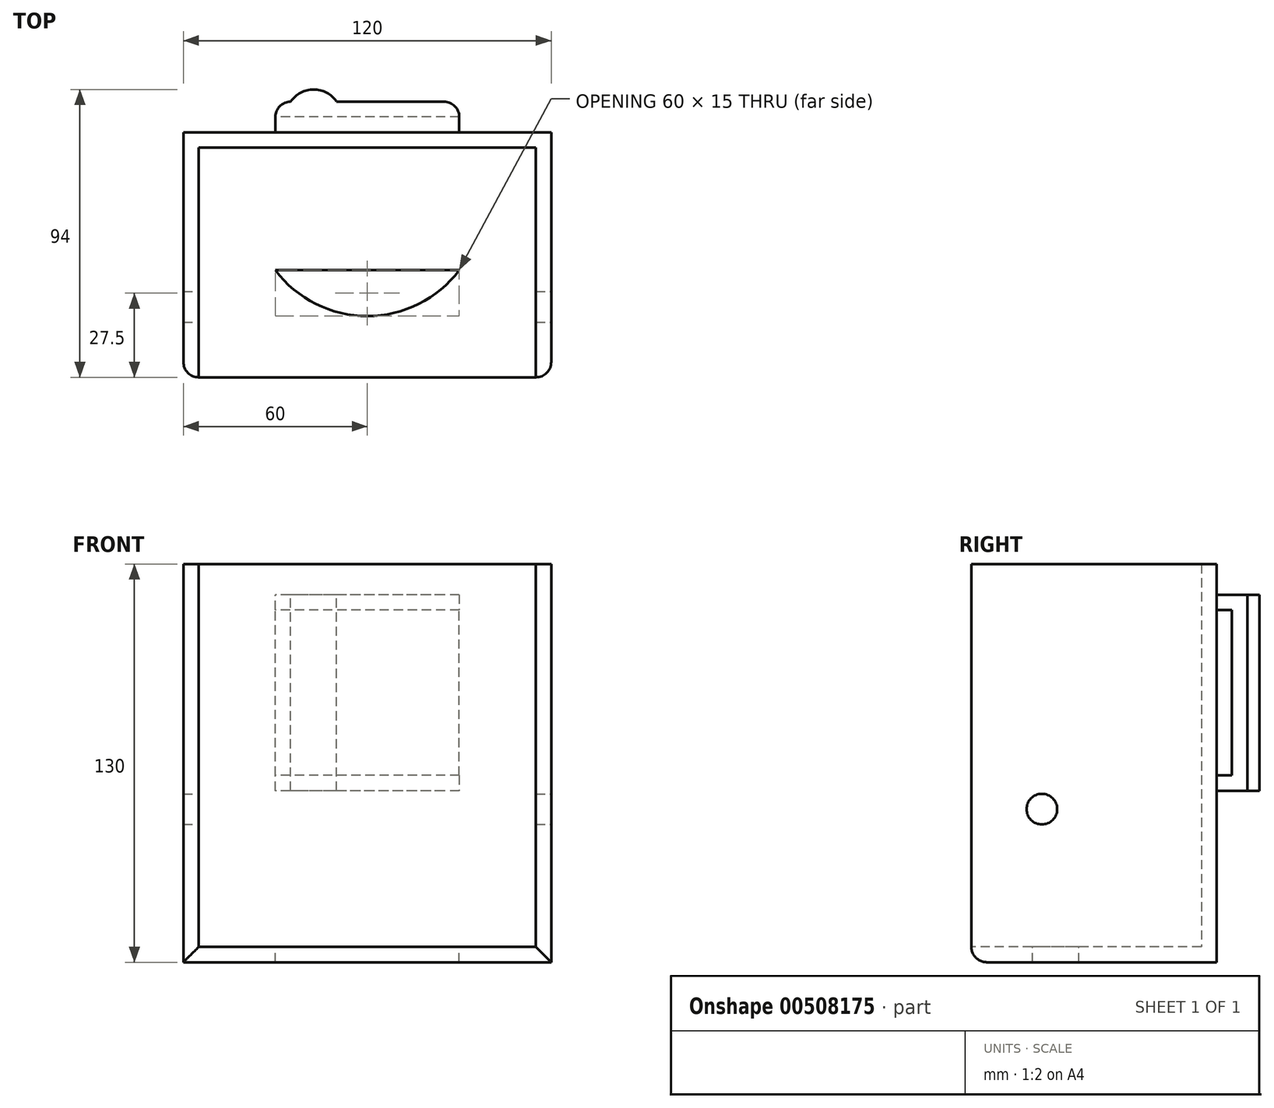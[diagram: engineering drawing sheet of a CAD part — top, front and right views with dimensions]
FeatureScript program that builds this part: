
annotation { "Feature Type Name" : "Feature", "Feature Type Description" : "" }
export const myFeature = defineFeature(function(context is Context, id is Id, definition is map)
    precondition{}
    {
        {
            var Q0;
            Q0=qCreatedBy(makeId("Top.planeOp"),FACE);
            var sketch = newSketch(context, id + "F0", { "sketchPlane" : qUnion([Q0])});
            skLineSegment(sketch, "E0.bottom", {"start": v(60, -40) * mm, "end": v(-60, -40) * mm});
            skLineSegment(sketch, "E0.top", {"start": v(60, 40) * mm, "end": v(-60, 40) * mm});
            skLineSegment(sketch, "E0.left", {"start": v(60, -40) * mm, "end": v(60, 40) * mm});
            skLineSegment(sketch, "E0.right", {"start": v(-60, -40) * mm, "end": v(-60, 40) * mm});
            skPoint(sketch, "E0.middle", {"position": v(0, 0) * mm});
            skLineSegment(sketch, "E1", {"start": v(-55, -40) * mm, "end": v(-55, 35) * mm});
            skLineSegment(sketch, "E2", {"start": v(-55, 35) * mm, "end": v(55, 35) * mm});
            skLineSegment(sketch, "E3", {"start": v(55, 35) * mm, "end": v(55, -40) * mm});
            skLineSegment(sketch, "E4", {"start": v(0, -5) * mm, "end": v(0, 35) * mm});
            skLineSegment(sketch, "E5", {"start": v(0, -5) * mm, "end": v(30, -5) * mm});
            skLineSegment(sketch, "E6", {"start": v(0, -5) * mm, "end": v(-30, -5) * mm});
            skLineSegment(sketch, "E7", {"start": v(0, -40) * mm, "end": v(0, -20) * mm});
            skArc(sketch, "E8", {"start": v(-30, -5) * mm, "mid": v(0, -20) * mm, "end": v(30, -5) * mm});
            skSolve(sketch);
        }
        {
            var Q0;
            Q0=makeQuery(id+"F0.imprint","IMPRINT",FACE,{"disambiguationData":[TD([[makeQuery(id+"F0.imprint","IMPRINT",EDGE,{"derivedFrom":sQuery(id+"F0.wireOp",EDGE,"E0.top")}),1.0]])]});
            var Q1;
            {var subQ0=sQuery(id+"F0.wireOp",EDGE,"E1");Q1=makeQuery(id+"F0.imprint","IMPRINT",FACE,{"disambiguationData":[TD([[makeQuery(id+"F0.imprint","IMPRINT",EDGE,{"derivedFrom":subQ0}),-1.0]])]});}
            var Q2;
            {var subQ0=sQuery(id+"F0.wireOp",EDGE,"E3");Q2=makeQuery(id+"F0.imprint","IMPRINT",FACE,{"disambiguationData":[TD([[makeQuery(id+"F0.imprint","IMPRINT",EDGE,{"derivedFrom":subQ0}),-1.0]])]});}
            extrude(context, id + "F1", {"entities" : qUnion([Q0, Q1, Q2]), "oppositeDirection" : true, "depth" : 5 * mm});
        }
        {
            var Q0;
            Q0=makeQuery(id+"F0.imprint","IMPRINT",FACE,{"disambiguationData":[TD([[makeQuery(id+"F0.imprint","IMPRINT",EDGE,{"derivedFrom":sQuery(id+"F0.wireOp",EDGE,"E0.top")}),1.0]])]});
            extrude(context, id + "F2", {"entities" : qUnion([Q0]), "operationType" : NewBodyOperationType.ADD, "depth" : 125 * mm});
        }
        {
            var Q0;
            Q0=makeQuery(id+"F2.opExtrude","SWEPT_FACE",FACE,{"disambiguationData":[OSD([sQuery(id+"F0.wireOp",EDGE,"E1")])]});
            var sketch = newSketch(context, id + "F3", { "sketchPlane" : qUnion([Q0])});
            skLineSegment(sketch, "E9.bottom", {"start": v(35, 0) * mm, "end": v(-17, 0) * mm});
            skLineSegment(sketch, "E9.top", {"start": v(35, 45) * mm, "end": v(-17, 45) * mm});
            skLineSegment(sketch, "E9.left", {"start": v(35, 0) * mm, "end": v(35, 45) * mm});
            skLineSegment(sketch, "E9.right", {"start": v(-17, 0) * mm, "end": v(-17, 45) * mm});
            skCircle(sketch, "E10", {"center": v(-17, 45) * mm, "radius": 5 * mm});
            skSolve(sketch);
        }
        {
            var Q0;
            {var subQ0=sQuery(id+"F3.wireOp",EDGE,"E9.right");var subQ1=sQuery(id+"F3.wireOp",EDGE,"E9.top");var subQ2=makeQuery(id+"F3.imprint","INTERSECT",VERTEX,{"derivedFrom":[subQ1,subQ0]});Q0=makeQuery(id+"F3.imprint","IMPRINT",FACE,{"disambiguationData":[TD([[makeQuery(id+"F3.imprint","IMPRINT",EDGE,{"disambiguationData":[TD([[subQ2,1.0]])],"derivedFrom":subQ1}),1.0]])]});}
            var Q1;
            {var subQ0=sQuery(id+"F3.wireOp",EDGE,"E9.right");var subQ1=sQuery(id+"F3.wireOp",EDGE,"E9.top");var subQ2=makeQuery(id+"F3.imprint","INTERSECT",VERTEX,{"derivedFrom":[subQ1,subQ0]});Q1=makeQuery(id+"F3.imprint","IMPRINT",FACE,{"disambiguationData":[TD([[makeQuery(id+"F3.imprint","IMPRINT",EDGE,{"disambiguationData":[TD([[subQ2,1.0]])],"derivedFrom":subQ1}),-1.0]])]});}
            extrude(context, id + "F4", {"entities" : qUnion([Q0, Q1]), "operationType" : NewBodyOperationType.REMOVE, "oppositeDirection" : true, "depth" : 25 * mm, "hasSecondDirection" : true, "secondDirectionOppositeDirection" : false, "secondDirectionDepth" : 129 * mm});
        }
        {
            var Q0;
            {var subQ0=sQuery(id+"F0.wireOp",EDGE,"E0.top");Q0=makeQuery(id+"F2.boolean.opBoolean","MERGE",FACE,{"derivedFrom":[makeQuery(id+"F1.opExtrude","SWEPT_FACE",FACE,{"disambiguationData":[OSD([subQ0])]}),makeQuery(id+"F2.opExtrude","SWEPT_FACE",FACE,{"disambiguationData":[OSD([subQ0])]})]});}
            var sketch = newSketch(context, id + "F5", { "sketchPlane" : qUnion([Q0])});
            skLineSegment(sketch, "E11", {"start": v(0, 125) * mm, "end": v(0, 115) * mm});
            skPoint(sketch, "E11.endSnap0", {"position": v(0, 125) * mm});
            skLineSegment(sketch, "E12", {"start": v(0, 115) * mm, "end": v(-30, 115) * mm});
            skLineSegment(sketch, "E13", {"start": v(0, 115) * mm, "end": v(30, 115) * mm});
            skLineSegment(sketch, "E14", {"start": v(-30, 115) * mm, "end": v(-30, 110) * mm});
            skLineSegment(sketch, "E15", {"start": v(-30, 110) * mm, "end": v(30, 110) * mm});
            skLineSegment(sketch, "E16", {"start": v(30, 110) * mm, "end": v(30, 115) * mm});
            skLineSegment(sketch, "E17", {"start": v(-30, 56) * mm, "end": v(30, 56) * mm});
            skLineSegment(sketch, "E18", {"start": v(-30, 56) * mm, "end": v(-30, 51) * mm});
            skLineSegment(sketch, "E19", {"start": v(-30, 51) * mm, "end": v(30, 51) * mm});
            skLineSegment(sketch, "E20", {"start": v(30, 51) * mm, "end": v(30, 56) * mm});
            skSolve(sketch);
        }
        {
            var Q0;
            Q0=makeQuery(id+"F5.imprint","IMPRINT",FACE,{"disambiguationData":[TD([[makeQuery(id+"F5.imprint","IMPRINT",EDGE,{"derivedFrom":sQuery(id+"F5.wireOp",EDGE,"E12")}),1.0]])]});
            var Q1;
            Q1=makeQuery(id+"F5.imprint","IMPRINT",FACE,{"disambiguationData":[TD([[makeQuery(id+"F5.imprint","IMPRINT",EDGE,{"derivedFrom":sQuery(id+"F5.wireOp",EDGE,"E17")}),-1.0]])]});
            extrude(context, id + "F6", {"entities" : qUnion([Q0, Q1]), "operationType" : NewBodyOperationType.ADD, "depth" : 10 * mm});
        }
        {
            var Q0;
            Q0=makeQuery(id+"F6.opExtrude","SWEPT_FACE",FACE,{"disambiguationData":[OSD([sQuery(id+"F5.wireOp",EDGE,"E15")])]});
            var sketch = newSketch(context, id + "F7", { "sketchPlane" : qUnion([Q0])});
            skLineSegment(sketch, "E21", {"start": v(30, -45) * mm, "end": v(-30, -45) * mm});
            skSolve(sketch);
        }
        {
            var Q0;
            {var subQ0=sQuery(id+"F7.wireOp",EDGE,"E21");Q0=makeQuery(id+"F7.imprint","IMPRINT",FACE,{"disambiguationData":[TD([[makeQuery(id+"F7.imprint","IMPRINT",EDGE,{"derivedFrom":subQ0}),1.0]])]});}
            extrude(context, id + "F8", {"entities" : qUnion([Q0]), "operationType" : NewBodyOperationType.ADD, "endBound" : BoundingType.UP_TO_NEXT, "depth" : 25 * mm});
        }
        {
            var Q0;
            {var subQ0=sQuery(id+"F0.wireOp",EDGE,"E0.right");var subQ1=sQuery(id+"F0.wireOp",EDGE,"E0.bottom");Q0=makeQuery(id+"F2.boolean.opBoolean","MERGE",EDGE,{"derivedFrom":[makeQuery(id+"F1.opExtrude","SWEPT_EDGE",EDGE,{"disambiguationData":[OSD([subQ1,subQ0])]}),makeQuery(id+"F2.opExtrude","SWEPT_EDGE",EDGE,{"disambiguationData":[OSD([subQ1,subQ0])]})]});}
            var Q1;
            Q1=makeQuery(id+"F1.opExtrude","CAP_EDGE",EDGE,{"disambiguationData":[OSD([sQuery(id+"F0.wireOp",EDGE,"E0.bottom")])],"isStart":false});
            var Q2;
            {var subQ0=sQuery(id+"F0.wireOp",EDGE,"E0.left");var subQ1=sQuery(id+"F0.wireOp",EDGE,"E0.bottom");Q2=makeQuery(id+"F2.boolean.opBoolean","MERGE",EDGE,{"derivedFrom":[makeQuery(id+"F1.opExtrude","SWEPT_EDGE",EDGE,{"disambiguationData":[OSD([subQ1,subQ0])]}),makeQuery(id+"F2.opExtrude","SWEPT_EDGE",EDGE,{"disambiguationData":[OSD([subQ1,subQ0])]})]});}
            var Q3;
            {var subQ0=sQuery(id+"F5.wireOp",EDGE,"E16");Q3=makeQuery(id+"F8.boolean.opBoolean","MERGE",EDGE,{"derivedFrom":[makeQuery(id+"F6.opExtrude","CAP_EDGE",EDGE,{"disambiguationData":[OSD([subQ0])],"isStart":false}),makeQuery(id+"F6.opExtrude","CAP_EDGE",EDGE,{"disambiguationData":[OSD([sQuery(id+"F5.wireOp",EDGE,"E20")])],"isStart":false}),makeQuery(id+"F8.opExtrude","SWEPT_EDGE",EDGE,{"disambiguationData":[OSD([sQuery(id+"F5.wireOp",EDGE,"E15"),subQ0])]})]});}
            var Q4;
            {var subQ0=sQuery(id+"F5.wireOp",EDGE,"E14");Q4=makeQuery(id+"F8.boolean.opBoolean","MERGE",EDGE,{"derivedFrom":[makeQuery(id+"F6.opExtrude","CAP_EDGE",EDGE,{"disambiguationData":[OSD([subQ0])],"isStart":false}),makeQuery(id+"F6.opExtrude","CAP_EDGE",EDGE,{"disambiguationData":[OSD([sQuery(id+"F5.wireOp",EDGE,"E18")])],"isStart":false}),makeQuery(id+"F8.opExtrude","SWEPT_EDGE",EDGE,{"disambiguationData":[OSD([subQ0,sQuery(id+"F5.wireOp",EDGE,"E15")])]})]});}
            fillet(context, id + "F9", {"entities" : qUnion([Q0, Q1, Q2, Q3, Q4]), "radius" : 5 * mm, "tangentPropagation" : true, "allowEdgeOverflow" : false});
        }
        {
            var Q0;
            Q0=makeQuery(id+"F6.opExtrude","SWEPT_FACE",FACE,{"disambiguationData":[OSD([sQuery(id+"F5.wireOp",EDGE,"E12"),sQuery(id+"F5.wireOp",EDGE,"E13")])]});
            var sketch = newSketch(context, id + "F10", { "sketchPlane" : qUnion([Q0])});
            skLineSegment(sketch, "E22", {"start": v(-25, 50) * mm, "end": v(-10, 50) * mm});
            skLineSegment(sketch, "E23", {"start": v(-17.5, 50) * mm, "end": v(-17.5, 54) * mm});
            skArc(sketch, "E24", {"start": v(-10, 50) * mm, "mid": v(-17.5, 54) * mm, "end": v(-25, 50) * mm});
            skLineSegment(sketch, "E25", {"start": v(0, 50) * mm, "end": v(0, 60.35) * mm});
            skArc(sketch, "E26.MirrorCS", {"start": v(10, 50) * mm, "mid": v(17.5, 54) * mm, "end": v(25, 50) * mm});
            skSolve(sketch);
        }
        {
            var Q0;
            {var subQ4=sQuery(id+"F10.wireOp",EDGE,"E23");Q0=makeQuery(id+"F10.imprint","IMPRINT",FACE,{"disambiguationData":[TD([[makeQuery(id+"F10.imprint","IMPRINT",EDGE,{"derivedFrom":subQ4}),1.0]])]});}
            var Q1;
            {var subQ3=sQuery(id+"F10.wireOp",EDGE,"E23");Q1=makeQuery(id+"F10.imprint","IMPRINT",FACE,{"disambiguationData":[TD([[makeQuery(id+"F10.imprint","IMPRINT",EDGE,{"derivedFrom":subQ3}),-1.0]])]});}
            var Q2;
            {var subQ0=sQuery(id+"F10.wireOp",EDGE,"E26.MirrorCS");Q2=makeQuery(id+"F10.imprint","IMPRINT",FACE,{"disambiguationData":[TD([[makeQuery(id+"F10.imprint","IMPRINT",EDGE,{"derivedFrom":subQ0}),-1.0]])]});}
            var Q3;
            Q3=makeQuery(id+"F6.opExtrude","SWEPT_FACE",FACE,{"disambiguationData":[OSD([sQuery(id+"F5.wireOp",EDGE,"E19")])]});
            extrude(context, id + "F11", {"entities" : qUnion([Q0, Q1, Q2]), "operationType" : NewBodyOperationType.ADD, "endBound" : BoundingType.UP_TO_SURFACE, "oppositeDirection" : true, "endBoundEntityFace" : qUnion([Q3]), "depth" : 25 * mm});
        }
    });
